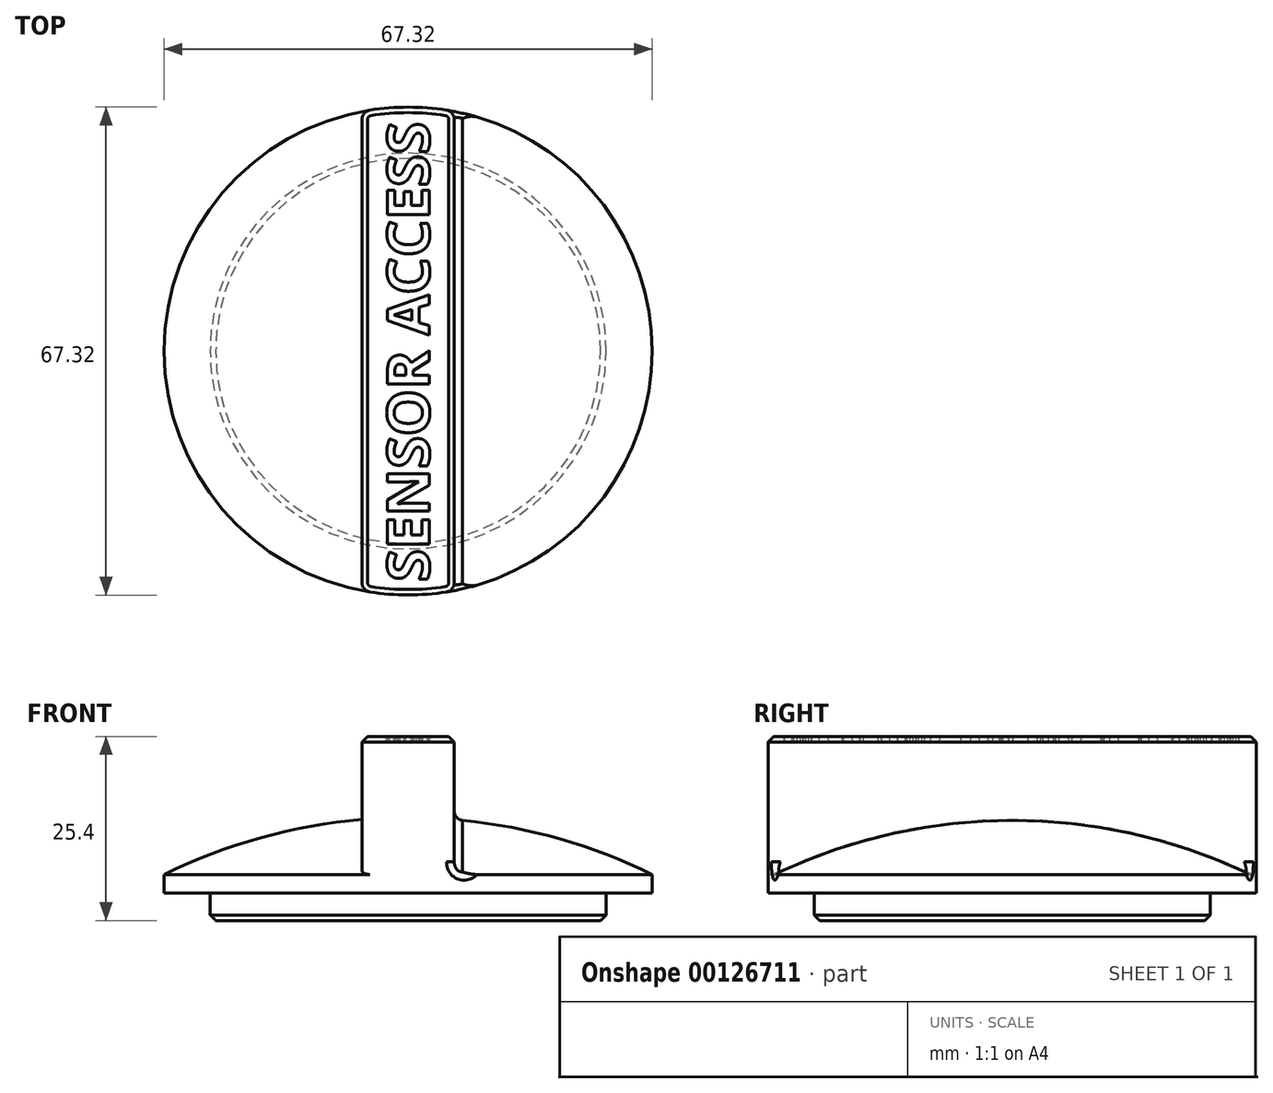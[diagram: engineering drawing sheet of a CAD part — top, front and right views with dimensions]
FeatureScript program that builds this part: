
annotation { "Feature Type Name" : "Feature", "Feature Type Description" : "" }
export const myFeature = defineFeature(function(context is Context, id is Id, definition is map)
    precondition{}
    {
        {
            var Q0;
            Q0=qCreatedBy(makeId("Right.planeOp"),FACE);
            var sketch = newSketch(context, id + "F0", { "sketchPlane" : qUnion([Q0])});
            skLineSegment(sketch, "E0", {"start": v(0, 0) * mm, "end": v(27.3, 0) * mm});
            skLineSegment(sketch, "E1", {"start": v(27.3, 0) * mm, "end": v(27.3, 3.81) * mm});
            skLineSegment(sketch, "E2", {"start": v(27.3, 3.81) * mm, "end": v(33.66, 3.81) * mm});
            skLineSegment(sketch, "E3", {"start": v(0, 0) * mm, "end": v(0, 31.75) * mm, "construction": true});
            skLineSegment(sketch, "E4", {"start": v(33.66, 3.81) * mm, "end": v(33.66, 6.35) * mm});
            skArc(sketch, "E5", {"start": v(33.65, 6.35) * mm, "mid": v(17.28, 12.2) * mm, "end": v(0, 14.18) * mm});
            skLineSegment(sketch, "E6", {"start": v(0, 14.18) * mm, "end": v(0, 0) * mm});
            skSolve(sketch);
        }
        {
            var Q0;
            Q0=makeQuery(id+"F0.imprint","IMPRINT",FACE,{"disambiguationData":[TD([[makeQuery(id+"F0.imprint","IMPRINT",EDGE,{"derivedFrom":sQuery(id+"F0.wireOp",EDGE,"E0")}),1.0]])]});
            var Q1;
            Q1=sQuery(id+"F0.wireOp",EDGE,"E3");
            revolve(context, id + "F1", {"entities" : qUnion([Q0]), "axis" : qUnion([Q1]), "revolveType" : RevolveType.FULL});
        }
        {
            var Q0;
            Q0=qCreatedBy(makeId("Top.planeOp"),FACE);
            cPlane(context, id + "F2", {"entities" : qUnion([Q0]), "cplaneType" : CPlaneType.OFFSET, "offset" : 25.4 * mm, "width" : 152.4 * mm, "height" : 152.4 * mm});
        }
        {
            var Q0;
            Q0=qCreatedBy(id+"F2.planeOp",FACE);
            var sketch = newSketch(context, id + "F3", { "sketchPlane" : qUnion([Q0])});
            skCircle(sketch, "E7.0", {"center": v(0, 0) * mm, "radius": 33.66 * mm, "construction": true});
            skLineSegment(sketch, "E8.left", {"start": v(-6.35, -33.05) * mm, "end": v(-6.35, 33.05) * mm});
            skLineSegment(sketch, "E8.right", {"start": v(6.35, -33.05) * mm, "end": v(6.35, 33.05) * mm});
            skArc(sketch, "E9", {"start": v(-6.35, -33.05) * mm, "mid": v(0, -33.65) * mm, "end": v(6.35, -33.05) * mm});
            skArc(sketch, "E10", {"start": v(-6.35, 33.05) * mm, "mid": v(0, 33.65) * mm, "end": v(6.35, 33.05) * mm});
            skText(sketch, "E11", { "text": "SENSOR ACCESS", "fontName": "OpenSans-Bold.ttf"});
            const initialGuessF3  = {"E11": [0.00292, -0.03181, 0, 1, 0.00584]};
            skSetInitialGuess(sketch, initialGuessF3);
            skSolve(sketch);
        }
        {
            var Q0;
            Q0 = qSketchRegion(id + "F3", true);
            var Q1;
            Q1=makeQuery(id+"F3.imprint","IMPRINT",FACE,{"disambiguationData":[TD([[makeQuery(id+"F3.imprint","IMPRINT",EDGE,{"derivedFrom":sQuery(id+"F3.wireOp",EDGE,"E8.left")}),-1.0]])]});
            var Q2;
            Q2=makeQuery(id+"F3.imprint","IMPRINT",FACE,{"disambiguationData":[TD([[makeQuery(id+"F3.imprint","IMPRINT",EDGE,{"derivedFrom":sQuery(id+"F3.wireOp",EDGE,"E11.sketch_text.stroke-96")}),-1.0]])]});
            var Q3;
            Q3=makeQuery(id+"F3.imprint","IMPRINT",FACE,{"disambiguationData":[TD([[makeQuery(id+"F3.imprint","IMPRINT",EDGE,{"derivedFrom":sQuery(id+"F3.wireOp",EDGE,"E11.sketch_text.stroke-115")}),-1.0]])]});
            var Q4;
            Q4=makeQuery(id+"F3.imprint","IMPRINT",FACE,{"disambiguationData":[TD([[makeQuery(id+"F3.imprint","IMPRINT",EDGE,{"derivedFrom":sQuery(id+"F3.wireOp",EDGE,"E11.sketch_text.stroke-0")}),-1.0]])]});
            var Q5;
            Q5=makeQuery(id+"F3.imprint","IMPRINT",FACE,{"disambiguationData":[TD([[makeQuery(id+"F3.imprint","IMPRINT",EDGE,{"derivedFrom":sQuery(id+"F3.wireOp",EDGE,"E11.sketch_text.stroke-28")}),-1.0]])]});
            var Q6;
            Q6=makeQuery(id+"F3.imprint","IMPRINT",FACE,{"disambiguationData":[TD([[makeQuery(id+"F3.imprint","IMPRINT",EDGE,{"derivedFrom":sQuery(id+"F3.wireOp",EDGE,"E11.sketch_text.stroke-40")}),-1.0]])]});
            var Q7;
            Q7=makeQuery(id+"F3.imprint","IMPRINT",FACE,{"disambiguationData":[TD([[makeQuery(id+"F3.imprint","IMPRINT",EDGE,{"derivedFrom":sQuery(id+"F3.wireOp",EDGE,"E11.sketch_text.stroke-54")}),-1.0]])]});
            var Q8;
            Q8=makeQuery(id+"F3.imprint","IMPRINT",FACE,{"disambiguationData":[TD([[makeQuery(id+"F3.imprint","IMPRINT",EDGE,{"derivedFrom":sQuery(id+"F3.wireOp",EDGE,"E11.sketch_text.stroke-90")}),1.0]])]});
            var Q9;
            Q9=makeQuery(id+"F3.imprint","IMPRINT",FACE,{"disambiguationData":[TD([[makeQuery(id+"F3.imprint","IMPRINT",EDGE,{"derivedFrom":sQuery(id+"F3.wireOp",EDGE,"E11.sketch_text.stroke-127")}),-1.0]])]});
            var Q10;
            Q10=makeQuery(id+"F3.imprint","IMPRINT",FACE,{"disambiguationData":[TD([[makeQuery(id+"F3.imprint","IMPRINT",EDGE,{"derivedFrom":sQuery(id+"F3.wireOp",EDGE,"E11.sketch_text.stroke-142")}),-1.0]])]});
            var Q11;
            Q11=makeQuery(id+"F3.imprint","IMPRINT",FACE,{"disambiguationData":[TD([[makeQuery(id+"F3.imprint","IMPRINT",EDGE,{"derivedFrom":sQuery(id+"F3.wireOp",EDGE,"E11.sketch_text.stroke-157")}),-1.0]])]});
            var Q12;
            Q12=makeQuery(id+"F3.imprint","IMPRINT",FACE,{"disambiguationData":[TD([[makeQuery(id+"F3.imprint","IMPRINT",EDGE,{"derivedFrom":sQuery(id+"F3.wireOp",EDGE,"E11.sketch_text.stroke-169")}),-1.0]])]});
            var Q13;
            Q13=makeQuery(id+"F3.imprint","IMPRINT",FACE,{"disambiguationData":[TD([[makeQuery(id+"F3.imprint","IMPRINT",EDGE,{"derivedFrom":sQuery(id+"F3.wireOp",EDGE,"E11.sketch_text.stroke-197")}),-1.0]])]});
            var Q14;
            Q14=makeQuery(id+"F3.imprint","IMPRINT",FACE,{"disambiguationData":[TD([[makeQuery(id+"F3.imprint","IMPRINT",EDGE,{"derivedFrom":sQuery(id+"F3.wireOp",EDGE,"E11.sketch_text.stroke-82")}),-1.0]])]});
            var Q15;
            Q15=makeQuery(id+"F3.imprint","IMPRINT",FACE,{"disambiguationData":[TD([[makeQuery(id+"F3.imprint","IMPRINT",EDGE,{"derivedFrom":sQuery(id+"F3.wireOp",EDGE,"E11.sketch_text.stroke-96")}),1.0]])]});
            var Q16;
            Q16=makeQuery(id+"F3.imprint","IMPRINT",FACE,{"disambiguationData":[TD([[makeQuery(id+"F3.imprint","IMPRINT",EDGE,{"derivedFrom":sQuery(id+"F3.wireOp",EDGE,"E11.sketch_text.stroke-123")}),1.0]])]});
            var Q17;
            Q17=makeQuery(id+"F1.opRevolve","SWEPT_FACE",FACE,{"disambiguationData":[OSD([sQuery(id+"F0.wireOp",EDGE,"E5")])]});
            extrude(context, id + "F4", {"entities" : qUnion([Q0, Q1, Q2, Q3, Q4, Q5, Q6, Q7, Q8, Q9, Q10, Q11, Q12, Q13, Q14, Q15, Q16]), "operationType" : NewBodyOperationType.ADD, "endBound" : BoundingType.UP_TO_SURFACE, "oppositeDirection" : true, "endBoundEntityFace" : qUnion([Q17]), "depth" : 25.4 * mm});
        }
        {
            var Q0;
            Q0=makeQuery(id+"F3.imprint","IMPRINT",FACE,{"disambiguationData":[TD([[makeQuery(id+"F3.imprint","IMPRINT",EDGE,{"derivedFrom":sQuery(id+"F3.wireOp",EDGE,"E11.sketch_text.stroke-96")}),-1.0]])]});
            var Q1;
            Q1=makeQuery(id+"F3.imprint","IMPRINT",FACE,{"disambiguationData":[TD([[makeQuery(id+"F3.imprint","IMPRINT",EDGE,{"derivedFrom":sQuery(id+"F3.wireOp",EDGE,"E11.sketch_text.stroke-115")}),-1.0]])]});
            var Q2;
            Q2=makeQuery(id+"F3.imprint","IMPRINT",FACE,{"disambiguationData":[TD([[makeQuery(id+"F3.imprint","IMPRINT",EDGE,{"derivedFrom":sQuery(id+"F3.wireOp",EDGE,"E11.sketch_text.stroke-0")}),-1.0]])]});
            var Q3;
            Q3=makeQuery(id+"F3.imprint","IMPRINT",FACE,{"disambiguationData":[TD([[makeQuery(id+"F3.imprint","IMPRINT",EDGE,{"derivedFrom":sQuery(id+"F3.wireOp",EDGE,"E11.sketch_text.stroke-28")}),-1.0]])]});
            var Q4;
            Q4=makeQuery(id+"F3.imprint","IMPRINT",FACE,{"disambiguationData":[TD([[makeQuery(id+"F3.imprint","IMPRINT",EDGE,{"derivedFrom":sQuery(id+"F3.wireOp",EDGE,"E11.sketch_text.stroke-40")}),-1.0]])]});
            var Q5;
            Q5=makeQuery(id+"F3.imprint","IMPRINT",FACE,{"disambiguationData":[TD([[makeQuery(id+"F3.imprint","IMPRINT",EDGE,{"derivedFrom":sQuery(id+"F3.wireOp",EDGE,"E11.sketch_text.stroke-54")}),-1.0]])]});
            var Q6;
            Q6=makeQuery(id+"F3.imprint","IMPRINT",FACE,{"disambiguationData":[TD([[makeQuery(id+"F3.imprint","IMPRINT",EDGE,{"derivedFrom":sQuery(id+"F3.wireOp",EDGE,"E11.sketch_text.stroke-127")}),-1.0]])]});
            var Q7;
            Q7=makeQuery(id+"F3.imprint","IMPRINT",FACE,{"disambiguationData":[TD([[makeQuery(id+"F3.imprint","IMPRINT",EDGE,{"derivedFrom":sQuery(id+"F3.wireOp",EDGE,"E11.sketch_text.stroke-142")}),-1.0]])]});
            var Q8;
            Q8=makeQuery(id+"F3.imprint","IMPRINT",FACE,{"disambiguationData":[TD([[makeQuery(id+"F3.imprint","IMPRINT",EDGE,{"derivedFrom":sQuery(id+"F3.wireOp",EDGE,"E11.sketch_text.stroke-157")}),-1.0]])]});
            var Q9;
            Q9=makeQuery(id+"F3.imprint","IMPRINT",FACE,{"disambiguationData":[TD([[makeQuery(id+"F3.imprint","IMPRINT",EDGE,{"derivedFrom":sQuery(id+"F3.wireOp",EDGE,"E11.sketch_text.stroke-169")}),-1.0]])]});
            var Q10;
            Q10=makeQuery(id+"F3.imprint","IMPRINT",FACE,{"disambiguationData":[TD([[makeQuery(id+"F3.imprint","IMPRINT",EDGE,{"derivedFrom":sQuery(id+"F3.wireOp",EDGE,"E11.sketch_text.stroke-197")}),-1.0]])]});
            var Q11;
            Q11=makeQuery(id+"F3.imprint","IMPRINT",FACE,{"disambiguationData":[TD([[makeQuery(id+"F3.imprint","IMPRINT",EDGE,{"derivedFrom":sQuery(id+"F3.wireOp",EDGE,"E11.sketch_text.stroke-82")}),-1.0]])]});
            extrude(context, id + "F5", {"entities" : qUnion([Q0, Q1, Q2, Q3, Q4, Q5, Q6, Q7, Q8, Q9, Q10, Q11]), "operationType" : NewBodyOperationType.REMOVE, "oppositeDirection" : true, "depth" : 0.76 * mm});
        }
        {
            var Q0;
            Q0=makeQuery(id+"F4.opExtrude","SWEPT_EDGE",EDGE,{"disambiguationData":[OSD([sQuery(id+"F3.wireOp",EDGE,"E8.right"),sQuery(id+"F3.wireOp",EDGE,"E9")])]});
            var Q1;
            Q1=makeQuery(id+"F4.opExtrude","SWEPT_EDGE",EDGE,{"disambiguationData":[OSD([sQuery(id+"F3.wireOp",EDGE,"E8.left"),sQuery(id+"F3.wireOp",EDGE,"E9")])]});
            var Q2;
            Q2=makeQuery(id+"F4.opExtrude","SWEPT_EDGE",EDGE,{"disambiguationData":[OSD([sQuery(id+"F3.wireOp",EDGE,"E8.right"),sQuery(id+"F3.wireOp",EDGE,"E10")])]});
            var Q3;
            Q3=makeQuery(id+"F4.opExtrude","CAP_EDGE",EDGE,{"disambiguationData":[OSD([sQuery(id+"F3.wireOp",EDGE,"E8.right")])],"isStart":false});
            var Q4;
            Q4=makeQuery(id+"F4.opExtrude","SWEPT_EDGE",EDGE,{"disambiguationData":[OSD([sQuery(id+"F3.wireOp",EDGE,"E8.left"),sQuery(id+"F3.wireOp",EDGE,"E10")])]});
            var Q5;
            Q5=makeQuery(id+"F4.opExtrude","CAP_EDGE",EDGE,{"disambiguationData":[OSD([sQuery(id+"F3.wireOp",EDGE,"E8.left")])],"isStart":false});
            fillet(context, id + "F6", {"entities" : qUnion([Q0, Q1, Q2, Q3, Q4, Q5]), "radius" : 1.27 * mm, "tangentPropagation" : true, "allowEdgeOverflow" : false});
        }
        {
            var Q0;
            Q0=makeQuery(id+"F4.opExtrude","CAP_EDGE",EDGE,{"disambiguationData":[OSD([sQuery(id+"F3.wireOp",EDGE,"E9")])],"isStart":true});
            chamfer(context, id + "F7", {"entities" : qUnion([Q0]), "width" : 0.76 * mm, "tangentPropagation" : true});
        }
        {
            var Q0;
            Q0=makeQuery(id+"F1.opRevolve","SWEPT_EDGE",EDGE,{"disambiguationData":[OSD([sQuery(id+"F0.wireOp",EDGE,"E0"),sQuery(id+"F0.wireOp",EDGE,"E1")])]});
            chamfer(context, id + "F8", {"entities" : qUnion([Q0]), "width" : 0.76 * mm, "tangentPropagation" : true});
        }
    });
